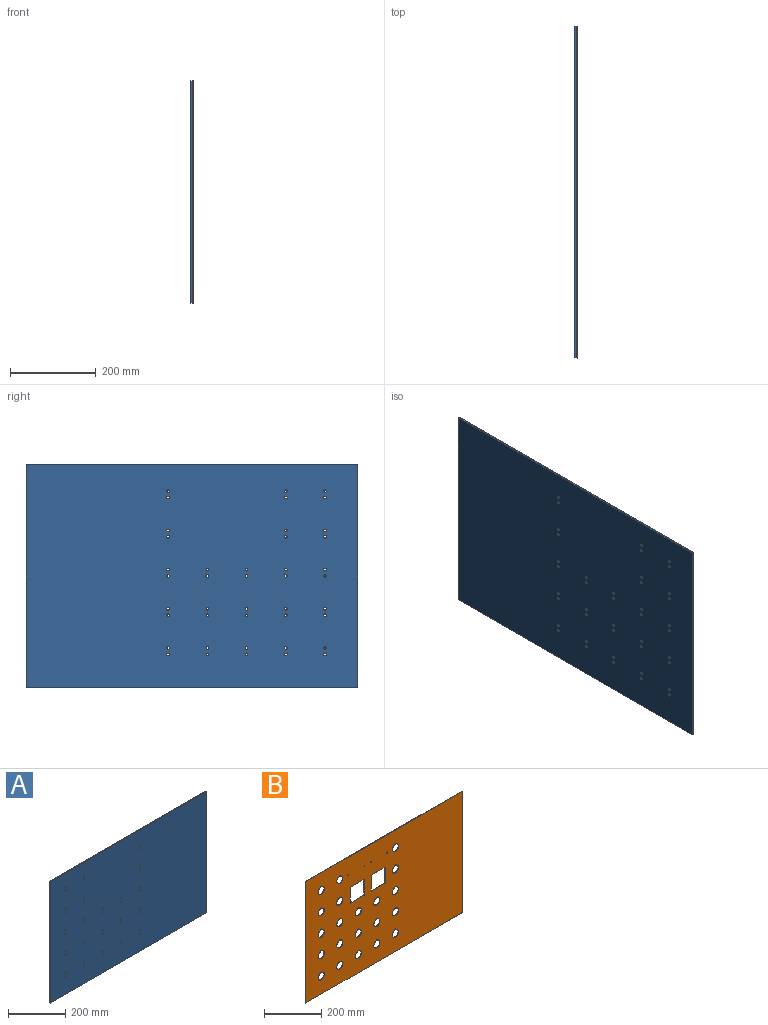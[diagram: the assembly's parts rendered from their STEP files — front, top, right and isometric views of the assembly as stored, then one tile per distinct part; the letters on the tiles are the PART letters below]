
ASSEMBLY  parts=2 mates=1
PART A: 48 faces, bbox 771.5x3.2x517.5 mm
  f0: plane 771.53x3.18mm, normal (0,0,1), area 2449.6mm2, adj f1,f45,f46,f47
  f1: plane 517.53x3.18mm, normal (-1,0,0), area 1643.1mm2, adj f0,f2,f46,f47
  f2: plane 771.53x3.18mm, normal (0,0,-1), area 2449.6mm2, adj f1,f45,f46,f47
  f3: cylinder r=3.09mm len=6.17mm, axis (0,1,0), area 61.6mm2, adj f46,f47
  f4: cylinder r=3.09mm len=6.17mm, axis (0,1,0), area 61.6mm2, adj f46,f47
  f5: cylinder r=3.09mm len=6.17mm, axis (0,1,0), area 61.6mm2, adj f46,f47
  f6: cylinder r=3.09mm len=6.17mm, axis (0,1,0), area 61.6mm2, adj f46,f47
  f7: cylinder r=3.09mm len=6.17mm, axis (0,1,0), area 61.6mm2, adj f46,f47
  f8: cylinder r=3.09mm len=6.17mm, axis (0,1,0), area 61.6mm2, adj f46,f47
  f9: cylinder r=3.09mm len=6.17mm, axis (0,1,0), area 61.6mm2, adj f46,f47
  f10: cylinder r=3.09mm len=6.17mm, axis (0,1,0), area 61.6mm2, adj f46,f47
  f11: cylinder r=3.09mm len=6.17mm, axis (0,1,0), area 61.6mm2, adj f46,f47
  f12: cylinder r=3.09mm len=6.17mm, axis (0,1,0), area 61.6mm2, adj f46,f47
  f13: cylinder r=3.09mm len=6.17mm, axis (0,1,0), area 61.6mm2, adj f46,f47
  f14: cylinder r=3.09mm len=6.17mm, axis (0,1,0), area 61.6mm2, adj f46,f47
  f15: cylinder r=3.09mm len=6.17mm, axis (0,1,0), area 61.6mm2, adj f46,f47
  f16: cylinder r=3.09mm len=6.17mm, axis (0,1,0), area 61.6mm2, adj f46,f47
  f17: cylinder r=3.09mm len=6.17mm, axis (0,1,0), area 61.6mm2, adj f46,f47
  f18: cylinder r=3.09mm len=6.17mm, axis (0,1,0), area 61.6mm2, adj f46,f47
  f19: cylinder r=3.09mm len=6.17mm, axis (0,1,0), area 61.6mm2, adj f46,f47
  f20: cylinder r=3.09mm len=6.17mm, axis (0,1,0), area 61.6mm2, adj f46,f47
  f21: cylinder r=3.09mm len=6.17mm, axis (0,1,0), area 61.6mm2, adj f46,f47
  f22: cylinder r=3.09mm len=6.17mm, axis (0,1,0), area 61.6mm2, adj f46,f47
  f23: cylinder r=3.09mm len=6.17mm, axis (0,1,0), area 61.6mm2, adj f46,f47
  f24: cylinder r=3.09mm len=6.17mm, axis (0,1,0), area 61.6mm2, adj f46,f47
  f25: cylinder r=3.09mm len=6.17mm, axis (0,1,0), area 61.6mm2, adj f46,f47
  f26: cylinder r=3.09mm len=6.17mm, axis (0,1,0), area 61.6mm2, adj f46,f47
  f27: cylinder r=3.09mm len=6.17mm, axis (0,1,0), area 61.6mm2, adj f46,f47
  f28: cylinder r=3.09mm len=6.17mm, axis (0,1,0), area 61.6mm2, adj f46,f47
  f29: cylinder r=3.09mm len=6.17mm, axis (0,1,0), area 61.6mm2, adj f46,f47
  f30: cylinder r=3.09mm len=6.17mm, axis (0,1,0), area 61.6mm2, adj f46,f47
  f31: cylinder r=3.09mm len=6.17mm, axis (0,1,0), area 61.6mm2, adj f46,f47
  f32: cylinder r=3.09mm len=6.17mm, axis (0,1,0), area 61.6mm2, adj f46,f47
  f33: cylinder r=3.09mm len=6.17mm, axis (0,1,0), area 61.6mm2, adj f46,f47
  f34: cylinder r=3.09mm len=6.17mm, axis (0,1,0), area 61.6mm2, adj f46,f47
  f35: cylinder r=3.09mm len=6.17mm, axis (0,1,0), area 61.6mm2, adj f46,f47
  f36: cylinder r=3.09mm len=6.17mm, axis (0,1,0), area 61.6mm2, adj f46,f47
  f37: cylinder r=3.09mm len=6.17mm, axis (0,1,0), area 61.6mm2, adj f46,f47
  f38: cylinder r=3.09mm len=6.17mm, axis (0,1,0), area 61.6mm2, adj f46,f47
  f39: cylinder r=3.09mm len=6.17mm, axis (0,1,0), area 61.6mm2, adj f46,f47
  f40: cylinder r=3.09mm len=6.17mm, axis (0,1,0), area 61.6mm2, adj f46,f47
  f41: cylinder r=3.09mm len=6.17mm, axis (0,1,0), area 61.6mm2, adj f46,f47
  f42: cylinder r=3.09mm len=6.17mm, axis (0,1,0), area 61.6mm2, adj f46,f47
  f43: cylinder r=3.09mm len=6.17mm, axis (0,1,0), area 61.6mm2, adj f46,f47
  f44: cylinder r=3.09mm len=6.17mm, axis (0,1,0), area 61.6mm2, adj f46,f47
  f45: plane 517.53x3.18mm, normal (1,0,0), area 1643.1mm2, adj f0,f2,f46,f47
  f46: plane 771.53x517.53mm, normal (0,-1,0), area 398026.8mm2, adj f0,f1,f2,f3,f4,f5,f6,f7
  f47: plane 771.53x517.53mm, normal (0,1,0), area 398026.8mm2, adj f0,f1,f2,f3,f4,f5,f6,f7
PART B: 60 faces, bbox 771.5x1.7x517.5 mm
  f0: plane 771.53x1.65mm, normal (0,0,1), area 1273.8mm2, adj f1,f57,f58,f59
  f1: plane 517.53x1.65mm, normal (-1,0,0), area 854.4mm2, adj f0,f2,f58,f59
  f2: plane 771.53x1.65mm, normal (0,0,-1), area 1273.8mm2, adj f1,f57,f58,f59
  f3: plane 68x1.65mm, normal (1,0,0), area 112.3mm2, adj f4,f30,f58,f59
  f4: plane 68x1.65mm, normal (0,0,-1), area 112.3mm2, adj f3,f5,f58,f59
  f5: plane 68x1.65mm, normal (-1,0,0), area 112.3mm2, adj f4,f30,f58,f59
  f6: plane 68x1.65mm, normal (1,0,0), area 112.3mm2, adj f7,f31,f58,f59
  f7: plane 68x1.65mm, normal (0,0,-1), area 112.3mm2, adj f6,f8,f58,f59
  f8: plane 68x1.65mm, normal (-1,0,0), area 112.3mm2, adj f7,f31,f58,f59
  f9: cylinder r=15mm len=30mm, axis (0,1,0), area 145.4mm2, adj f32,f58,f59
  f10: cylinder r=15mm len=30mm, axis (0,1,0), area 145.4mm2, adj f33,f58,f59
  f11: cylinder r=15mm len=30mm, axis (0,1,0), area 145.4mm2, adj f34,f58,f59
  f12: cylinder r=15mm len=30mm, axis (0,1,0), area 145.4mm2, adj f35,f58,f59
  f13: cylinder r=15mm len=30mm, axis (0,1,0), area 145.4mm2, adj f36,f58,f59
  f14: cylinder r=15mm len=30mm, axis (0,1,0), area 145.4mm2, adj f37,f58,f59
  f15: cylinder r=15mm len=30mm, axis (0,1,0), area 145.4mm2, adj f38,f58,f59
  f16: cylinder r=15mm len=30mm, axis (0,1,0), area 145.4mm2, adj f39,f58,f59
  f17: cylinder r=15mm len=30mm, axis (0,1,0), area 145.4mm2, adj f40,f58,f59
  f18: cylinder r=15mm len=30mm, axis (0,1,0), area 145.4mm2, adj f41,f58,f59
  f19: cylinder r=15mm len=30mm, axis (0,1,0), area 145.4mm2, adj f42,f58,f59
  f20: cylinder r=15mm len=30mm, axis (0,1,0), area 145.4mm2, adj f43,f58,f59
  f21: cylinder r=15mm len=30mm, axis (0,1,0), area 145.4mm2, adj f44,f58,f59
  f22: cylinder r=15mm len=30mm, axis (0,1,0), area 145.4mm2, adj f45,f58,f59
  f23: cylinder r=15mm len=30mm, axis (0,1,0), area 145.4mm2, adj f46,f58,f59
  f24: cylinder r=15mm len=30mm, axis (0,1,0), area 145.4mm2, adj f47,f58,f59
  f25: cylinder r=15mm len=30mm, axis (0,1,0), area 145.4mm2, adj f48,f58,f59
  f26: cylinder r=15mm len=30mm, axis (0,1,0), area 145.4mm2, adj f49,f58,f59
  f27: cylinder r=15mm len=30mm, axis (0,1,0), area 145.4mm2, adj f50,f58,f59
  f28: cylinder r=15mm len=30mm, axis (0,1,0), area 145.4mm2, adj f51,f58,f59
  f29: cylinder r=15mm len=30mm, axis (0,1,0), area 145.4mm2, adj f52,f58,f59
  f30: plane 68x1.65mm, normal (0,0,1), area 112.3mm2, adj f3,f5,f58,f59
  f31: plane 68x1.65mm, normal (0,0,1), area 112.3mm2, adj f6,f8,f58,f59
  f32: cylinder r=3.09mm len=6.17mm, axis (0,1,0), area 17.1mm2, adj f9,f58,f59
  f33: cylinder r=3.09mm len=6.17mm, axis (0,1,0), area 17.1mm2, adj f10,f58,f59
  f34: cylinder r=3.09mm len=6.17mm, axis (0,1,0), area 17.1mm2, adj f11,f58,f59
  f35: cylinder r=3.09mm len=6.17mm, axis (0,1,0), area 17.1mm2, adj f12,f58,f59
  f36: cylinder r=3.09mm len=6.17mm, axis (0,1,0), area 17.1mm2, adj f13,f58,f59
  f37: cylinder r=3.09mm len=6.17mm, axis (0,1,0), area 17.1mm2, adj f14,f58,f59
  f38: cylinder r=3.09mm len=6.17mm, axis (0,1,0), area 17.1mm2, adj f15,f58,f59
  f39: cylinder r=3.09mm len=6.17mm, axis (0,1,0), area 17.1mm2, adj f16,f58,f59
  f40: cylinder r=3.09mm len=6.17mm, axis (0,1,0), area 17.1mm2, adj f17,f58,f59
  f41: cylinder r=3.09mm len=6.17mm, axis (0,1,0), area 17.1mm2, adj f18,f58,f59
  f42: cylinder r=3.09mm len=6.17mm, axis (0,1,0), area 17.1mm2, adj f19,f58,f59
  f43: cylinder r=3.09mm len=6.17mm, axis (0,1,0), area 17.1mm2, adj f20,f58,f59
  f44: cylinder r=3.09mm len=6.17mm, axis (0,1,0), area 17.1mm2, adj f21,f58,f59
  f45: cylinder r=3.09mm len=6.17mm, axis (0,1,0), area 17.1mm2, adj f22,f58,f59
  f46: cylinder r=3.09mm len=6.17mm, axis (0,1,0), area 17.1mm2, adj f23,f58,f59
  f47: cylinder r=3.09mm len=6.17mm, axis (0,1,0), area 17.1mm2, adj f24,f58,f59
  f48: cylinder r=3.09mm len=6.17mm, axis (0,1,0), area 17.1mm2, adj f25,f58,f59
  f49: cylinder r=3.09mm len=6.17mm, axis (0,1,0), area 17.1mm2, adj f26,f58,f59
  f50: cylinder r=3.09mm len=6.17mm, axis (0,1,0), area 17.1mm2, adj f27,f58,f59
  f51: cylinder r=3.09mm len=6.17mm, axis (0,1,0), area 17.1mm2, adj f28,f58,f59
  f52: cylinder r=3.09mm len=6.17mm, axis (0,1,0), area 17.1mm2, adj f29,f58,f59
  f53: cylinder r=1.68mm len=3.35mm, axis (0,1,0), area 17.4mm2, adj f58,f59
  f54: cylinder r=1.68mm len=3.35mm, axis (0,1,0), area 17.4mm2, adj f58,f59
  f55: cylinder r=1.68mm len=3.35mm, axis (0,1,0), area 17.4mm2, adj f58,f59
  f56: cylinder r=1.68mm len=3.35mm, axis (0,1,0), area 17.4mm2, adj f58,f59
  f57: plane 517.53x1.65mm, normal (1,0,0), area 854.4mm2, adj f0,f2,f58,f59
  f58: plane 771.53x517.53mm, normal (0,-1,0), area 374832mm2, adj f0,f1,f2,f3,f4,f5,f6,f7
  f59: plane 771.53x517.53mm, normal (0,1,0), area 374832mm2, adj f0,f1,f2,f3,f4,f5,f6,f7
PLACE A rot(axis=(0,0,1),90deg) t=(-391.59,662.45,-130.32)mm
PLACE B rot(axis=(0,0,1),90deg) t=(-388.42,845.53,-192.67)mm
MATE fastened A.f0 <-> B.f0  axis (0,0,1) through (-388.42,122.65,267.45)mm
